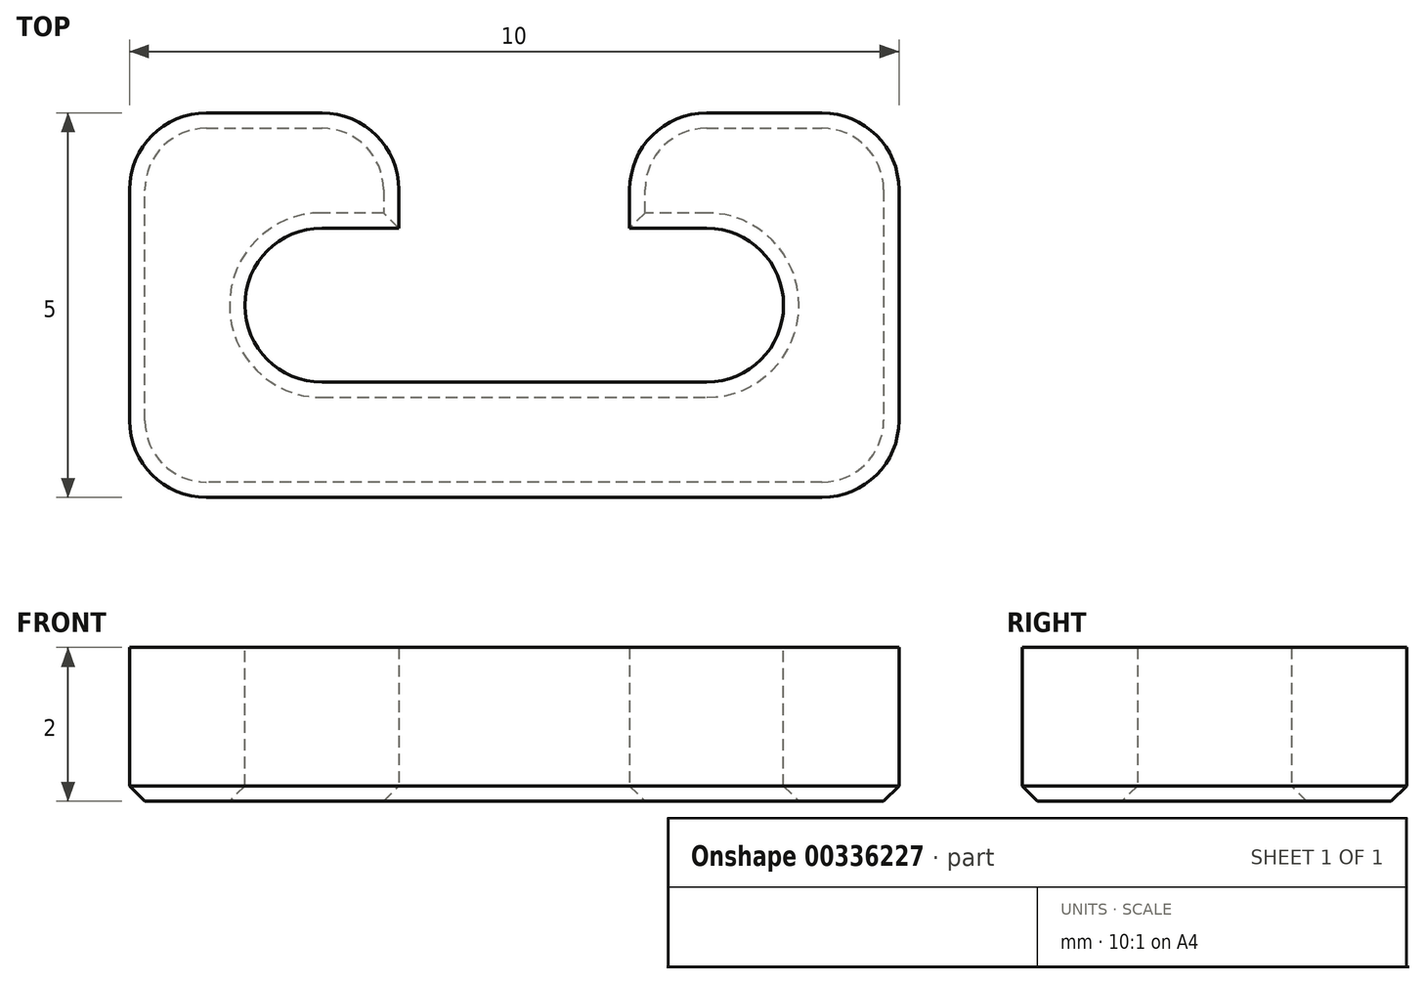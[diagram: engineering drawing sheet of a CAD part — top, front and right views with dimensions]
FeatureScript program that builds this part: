
annotation { "Feature Type Name" : "Feature", "Feature Type Description" : "" }
export const myFeature = defineFeature(function(context is Context, id is Id, definition is map)
    precondition{}
    {
        {
            var Q0;
            Q0=qCreatedBy(makeId("Top.planeOp"),FACE);
            var sketch = newSketch(context, id + "F0", { "sketchPlane" : qUnion([Q0])});
            skLineSegment(sketch, "E0", {"start": v(0, 0) * mm, "end": v(-3.5, 0) * mm});
            skLineSegment(sketch, "E1", {"start": v(-3.5, 0) * mm, "end": v(-3.5, 2) * mm});
            skLineSegment(sketch, "E2", {"start": v(-3.5, 2) * mm, "end": v(-1.5, 2) * mm});
            skLineSegment(sketch, "E3", {"start": v(-1.5, 2) * mm, "end": v(-1.5, 3.5) * mm});
            skLineSegment(sketch, "E4", {"start": v(-1.5, 3.5) * mm, "end": v(-5, 3.5) * mm});
            skLineSegment(sketch, "E5", {"start": v(-5, 3.5) * mm, "end": v(-5, -1.5) * mm});
            skLineSegment(sketch, "E6", {"start": v(-5, -1.5) * mm, "end": v(0, -1.5) * mm});
            skLineSegment(sketch, "E7.MirrorCS", {"start": v(1.5, 2) * mm, "end": v(1.5, 3.5) * mm});
            skLineSegment(sketch, "E8.MirrorCS", {"start": v(1.5, 3.5) * mm, "end": v(5, 3.5) * mm});
            skLineSegment(sketch, "E9.MirrorCS", {"start": v(5, 3.5) * mm, "end": v(5, -1.5) * mm});
            skLineSegment(sketch, "E10.MirrorCS", {"start": v(5, -1.5) * mm, "end": v(0, -1.5) * mm});
            skLineSegment(sketch, "E11.MirrorCS", {"start": v(0, 0) * mm, "end": v(3.5, 0) * mm});
            skLineSegment(sketch, "E12.MirrorCS", {"start": v(3.5, 0) * mm, "end": v(3.5, 2) * mm});
            skLineSegment(sketch, "E13.MirrorCS", {"start": v(3.5, 2) * mm, "end": v(1.5, 2) * mm});
            skSolve(sketch);
        }
        {
            var Q0;
            Q0 = qSketchRegion(id + "F0", true);
            extrude(context, id + "F1", {"entities" : qUnion([Q0]), "depth" : 2 * mm});
        }
        {
            var Q0;
            Q0=makeQuery(id+"F1.opExtrude","SWEPT_EDGE",EDGE,{"disambiguationData":[OSD([sQuery(id+"F0.wireOp",EDGE,"E3"),sQuery(id+"F0.wireOp",EDGE,"E4")])]});
            var Q1;
            Q1=makeQuery(id+"F1.opExtrude","SWEPT_EDGE",EDGE,{"disambiguationData":[OSD([sQuery(id+"F0.wireOp",EDGE,"E7.MirrorCS"),sQuery(id+"F0.wireOp",EDGE,"E8.MirrorCS")])]});
            var Q2;
            Q2=makeQuery(id+"F1.opExtrude","SWEPT_EDGE",EDGE,{"disambiguationData":[OSD([sQuery(id+"F0.wireOp",EDGE,"E8.MirrorCS"),sQuery(id+"F0.wireOp",EDGE,"E9.MirrorCS")])]});
            var Q3;
            Q3=makeQuery(id+"F1.opExtrude","SWEPT_EDGE",EDGE,{"disambiguationData":[OSD([sQuery(id+"F0.wireOp",EDGE,"E9.MirrorCS"),sQuery(id+"F0.wireOp",EDGE,"E10.MirrorCS")])]});
            var Q4;
            Q4=makeQuery(id+"F1.opExtrude","SWEPT_EDGE",EDGE,{"disambiguationData":[OSD([sQuery(id+"F0.wireOp",EDGE,"E5"),sQuery(id+"F0.wireOp",EDGE,"E6")])]});
            var Q5;
            Q5=makeQuery(id+"F1.opExtrude","SWEPT_EDGE",EDGE,{"disambiguationData":[OSD([sQuery(id+"F0.wireOp",EDGE,"E4"),sQuery(id+"F0.wireOp",EDGE,"E5")])]});
            var Q6;
            Q6=makeQuery(id+"F1.opExtrude","SWEPT_EDGE",EDGE,{"disambiguationData":[OSD([sQuery(id+"F0.wireOp",EDGE,"E1"),sQuery(id+"F0.wireOp",EDGE,"E2")])]});
            var Q7;
            Q7=makeQuery(id+"F1.opExtrude","SWEPT_EDGE",EDGE,{"disambiguationData":[OSD([sQuery(id+"F0.wireOp",EDGE,"E0"),sQuery(id+"F0.wireOp",EDGE,"E1")])]});
            var Q8;
            Q8=makeQuery(id+"F1.opExtrude","SWEPT_EDGE",EDGE,{"disambiguationData":[OSD([sQuery(id+"F0.wireOp",EDGE,"E12.MirrorCS"),sQuery(id+"F0.wireOp",EDGE,"E13.MirrorCS")])]});
            var Q9;
            Q9=makeQuery(id+"F1.opExtrude","SWEPT_EDGE",EDGE,{"disambiguationData":[OSD([sQuery(id+"F0.wireOp",EDGE,"E11.MirrorCS"),sQuery(id+"F0.wireOp",EDGE,"E12.MirrorCS")])]});
            fillet(context, id + "F2", {"entities" : qUnion([Q0, Q1, Q2, Q3, Q4, Q5, Q6, Q7, Q8, Q9]), "radius" : 1 * mm, "allowEdgeOverflow" : false});
        }
        {
            var Q0;
            Q0=makeQuery(id+"F1.opExtrude","CAP_FACE",FACE,{"disambiguationData":[OSD([sQuery(id+"F0.wireOp",EDGE,"E0"),sQuery(id+"F0.wireOp",EDGE,"E1"),sQuery(id+"F0.wireOp",EDGE,"E2"),sQuery(id+"F0.wireOp",EDGE,"E3"),sQuery(id+"F0.wireOp",EDGE,"E4"),sQuery(id+"F0.wireOp",EDGE,"E5"),sQuery(id+"F0.wireOp",EDGE,"E6"),sQuery(id+"F0.wireOp",EDGE,"E7.MirrorCS"),sQuery(id+"F0.wireOp",EDGE,"E8.MirrorCS"),sQuery(id+"F0.wireOp",EDGE,"E9.MirrorCS"),sQuery(id+"F0.wireOp",EDGE,"E10.MirrorCS"),sQuery(id+"F0.wireOp",EDGE,"E11.MirrorCS"),sQuery(id+"F0.wireOp",EDGE,"E12.MirrorCS"),sQuery(id+"F0.wireOp",EDGE,"E13.MirrorCS")])],"isStart":true});
            chamfer(context, id + "F3", {"entities" : qUnion([Q0]), "width" : .2 * mm});
        }
    });
